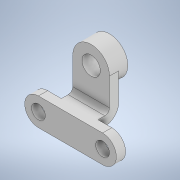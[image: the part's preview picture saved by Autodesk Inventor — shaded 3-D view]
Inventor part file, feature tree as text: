
AUTODESK INVENTOR PART (.ipt)
format: ipt  version: 2022.2 (Build 262287030, 287C)  size: 150,528 bytes
history: native  units: in
note: dims shown in document units (in); Inventor stores cm internally (conversion verified against a paired STEP export)
features: sketch x4, extrude x3, hole x2
ambient origin geometry x8: Origin, YZ Plane, XZ Plane, XY Plane, X Axis, Y Axis, Z Axis, Center Point
bodies: Solid1 (feature_tree)
feature tree (9):
  extrude  "Extrusion1"  Depth=2.0in TaperAngle=0.0deg
  extrude  "Extrusion2"  Depth=0.5in
  sketch  "Sketch3"  dims[d5=1.0in d6=1.5in]
  extrude  "Extrusion3"  Depth=1.5in
  hole  "Hole1"  [1 undecoded]
  hole  "Hole2"  [1 undecoded]
  sketch  "Sketch1"  dims[d0=4.0in d1=2.0in d2=0.0in]
  sketch  "Sketch2"  dims[d3=2.25in d4=0.5in]
  sketch  "Sketch4"  dims[d7=5.0in d8=4.0in d9=0.0in d10=1.5in d11=7.0in d12=5.0in d13=1.0in d14=0.0in d15=1.5in d16=0.75in d17=0.375in d18=0.25in d19=0.5635in d20=1.0in d21=0.8108in d22=2.0in d23=0.75in d24=0.375in d25=0.25in d26=0.5635in d27=1.0in d28=0.8108in]
note: 2 required parameter values undecoded (feature->parameter linkage not recoverable at this tier; creation-order binding heuristic only, values carry confidence <= 0.55)
